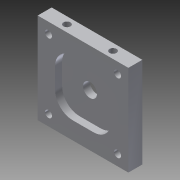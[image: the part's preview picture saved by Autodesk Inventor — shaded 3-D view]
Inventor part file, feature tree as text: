
AUTODESK INVENTOR PART (.ipt)
format: ipt  version: 2013 (Build 170138000, 138)  size: 133,120 bytes
history: native  units: in
note: dims shown in document units (in); Inventor stores cm internally (conversion verified against a paired STEP export)
features: extrude x4, sketch x4, fillet x2
ambient origin geometry x8: Origin, YZ Plane, XZ Plane, XY Plane, X Axis, Y Axis, Z Axis, Center Point
bodies: Solid1 (feature_tree)
feature tree (10):
  extrude  "Extrusion1"  Depth=1.625in
  extrude  "Extrusion2"  Depth=0.125in
  extrude  "Extrusion3"  Depth=0.125in
  fillet  "Fillet1"  Radius=0.125in
  fillet  "Fillet2"  Radius=0.8125in
  extrude  "Extrusion4"  Depth=0.25in TaperAngle=0.0deg
  sketch  "Sketch1"  dims[d0=1.625in d2=1.625in]
  sketch  "Sketch2"  dims[d3=1.75in d4=0.125in]
  sketch  "Sketch3"  dims[d5=0.125in d6=0.125in d7=0.125in d8=0.8125in]
  sketch  "Sketch4"  dims[d9=0.8125in d10=0.25in d11=0.0in d12=0.1257in d14=0.1257in d15=0.4in d17=0.4in d18=0.125in d19=0.125in d20=0.25in d21=0.0in d29=0.125in d30=0.0in d31=0.3125in d32=0.3125in d33=0.25in d34=1.0in d35=0.0in]
